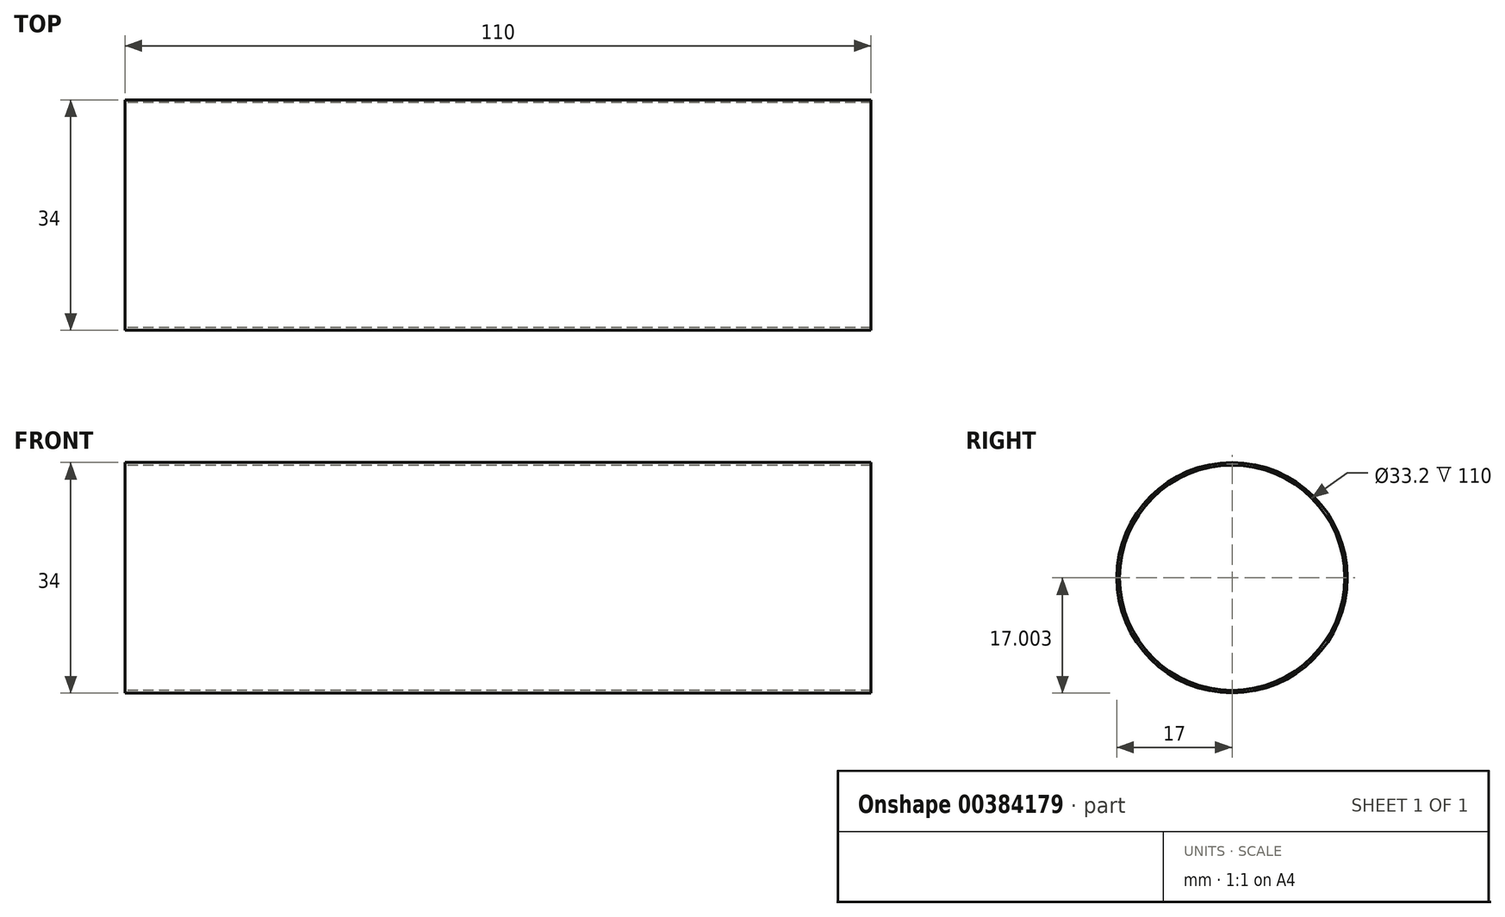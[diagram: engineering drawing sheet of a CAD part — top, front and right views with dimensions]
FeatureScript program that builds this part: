
annotation { "Feature Type Name" : "Feature", "Feature Type Description" : "" }
export const myFeature = defineFeature(function(context is Context, id is Id, definition is map)
    precondition{}
    {
        {
            var Q0;
            Q0=qCreatedBy(makeId("Front.planeOp"),FACE);
            var sketch = newSketch(context, id + "F0", { "sketchPlane" : qUnion([Q0])});
            skLineSegment(sketch, "E0.bottom", {"start": v(-2.43, 15.71) * mm, "end": v(107.57, 15.71) * mm});
            skLineSegment(sketch, "E0.top", {"start": v(-2.43, -1.29) * mm, "end": v(107.57, -1.29) * mm});
            skLineSegment(sketch, "E0.left", {"start": v(-2.43, 15.71) * mm, "end": v(-2.43, -1.29) * mm});
            skLineSegment(sketch, "E0.right", {"start": v(107.57, 15.71) * mm, "end": v(107.57, -1.29) * mm});
            skSolve(sketch);
        }
        {
            var Q0;
            Q0=makeQuery(id+"F0.imprint","IMPRINT",FACE,{"disambiguationData":[TD([[makeQuery(id+"F0.imprint","IMPRINT",EDGE,{"derivedFrom":sQuery(id+"F0.wireOp",EDGE,"E0.bottom")}),-1.0]])]});
            var Q1;
            Q1=sQuery(id+"F0.wireOp",EDGE,"E0.top");
            revolve(context, id + "F1", {"entities" : qUnion([Q0]), "axis" : qUnion([Q1]), "revolveType" : RevolveType.FULL});
        }
        {
            var Q0;
            Q0=makeQuery(id+"F1.opRevolve","SWEPT_FACE",FACE,{"disambiguationData":[OSD([sQuery(id+"F0.wireOp",EDGE,"E0.left")])]});
            var sketch = newSketch(context, id + "F2", { "sketchPlane" : qUnion([Q0])});
            skCircle(sketch, "E1", {"center": v(0, -1.29) * mm, "radius": 16.6 * mm});
            skSolve(sketch);
        }
        {
            var Q0;
            Q0=sQuery(id+"F2.wireOp",VERTEX,"E1.center");
            var Q1;
            Q1=makeQuery(id+"F1.opRevolve","SWEPT_BODY",BODY,{"disambiguationData":[OSD([sQuery(id+"F0.wireOp",EDGE,"E0.bottom"),sQuery(id+"F0.wireOp",EDGE,"E0.top"),sQuery(id+"F0.wireOp",EDGE,"E0.left"),sQuery(id+"F0.wireOp",EDGE,"E0.right")])]});
            hole(context, id + "F3", {"style" : HoleStyle.SIMPLE, "endStyle" : HoleEndStyle.BLIND, "holeDiameter" : 33.2 * mm, "holeDepth" : 110 * mm, "isTappedThrough" : true, "tappedDepth" : 12 * mm, "tapClearance" : 3, "locations" : qUnion([Q0]), "scope" : qUnion([Q1])});
        }
    });
